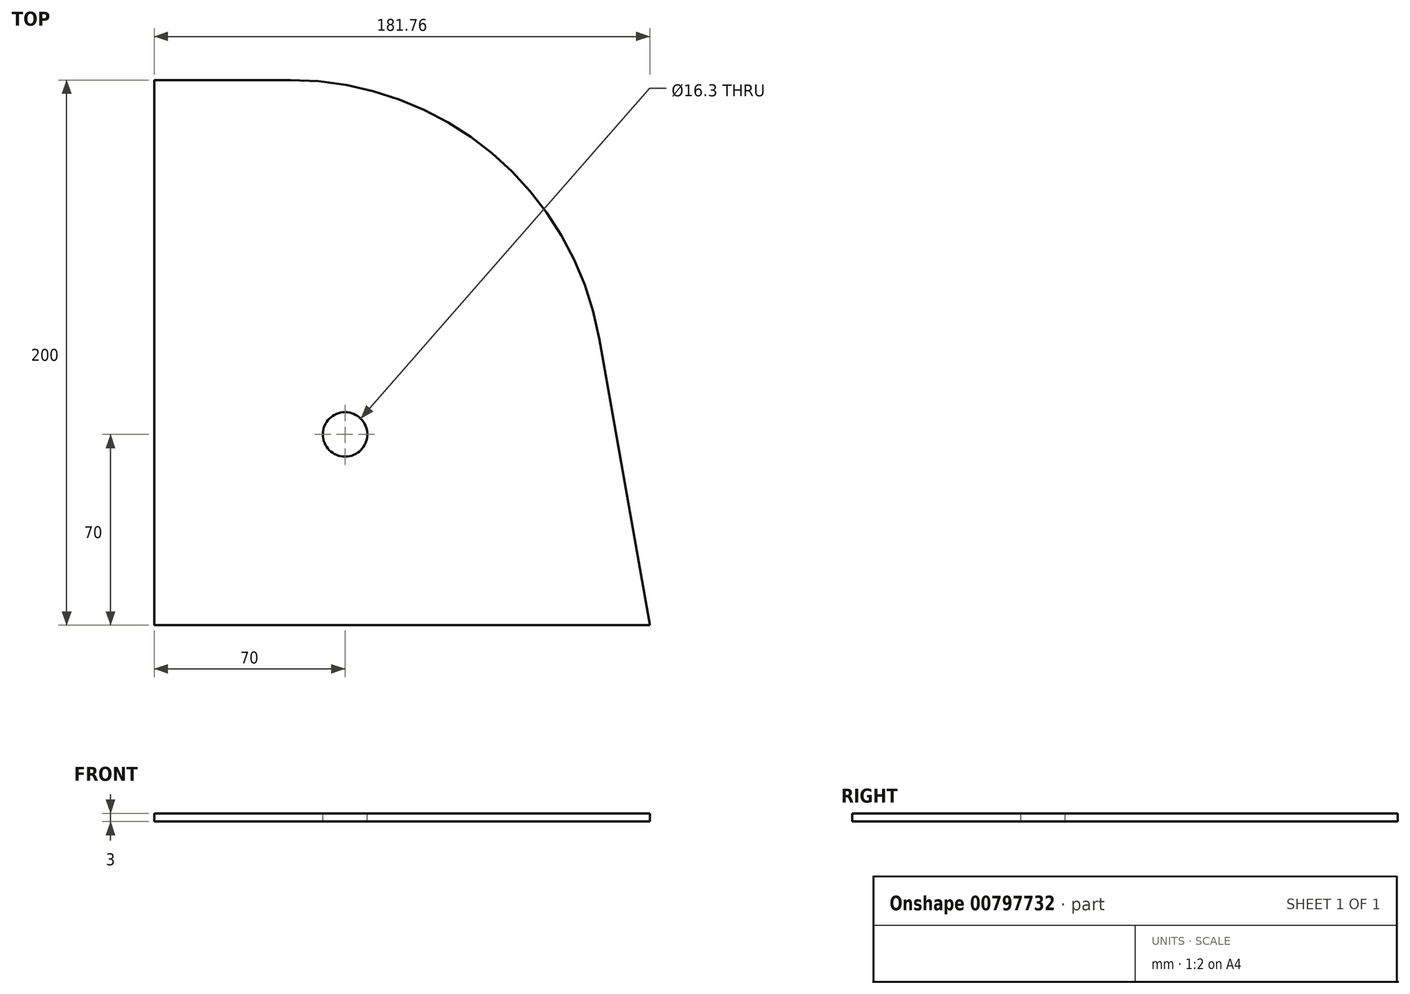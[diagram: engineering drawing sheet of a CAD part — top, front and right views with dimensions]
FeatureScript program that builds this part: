
annotation { "Feature Type Name" : "Feature", "Feature Type Description" : "" }
export const myFeature = defineFeature(function(context is Context, id is Id, definition is map)
    precondition{}
    {
        {
            var Q0;
            Q0=qCreatedBy(makeId("Top.planeOp"),FACE);
            var sketch = newSketch(context, id + "F0", { "sketchPlane" : qUnion([Q0])});
            skLineSegment(sketch, "E0", {"start": v(0, 0) * mm, "end": v(0, 200) * mm});
            skLineSegment(sketch, "E1", {"start": v(0, 0) * mm, "end": v(181.76, 0) * mm});
            skLineSegment(sketch, "E2", {"start": v(181.76, 0) * mm, "end": v(163.25, 104.97) * mm});
            skLineSegment(sketch, "E3", {"start": v(0, 200) * mm, "end": v(50, 200) * mm});
            skArc(sketch, "E4", {"start": v(163.25, 104.97) * mm, "mid": v(123.92, 173.1) * mm, "end": v(50, 200) * mm});
            skSolve(sketch);
        }
        {
            var Q0;
            Q0 = qSketchRegion(id + "F0", true);
            extrude(context, id + "F1", {"entities" : qUnion([Q0]), "depth" : 3 * mm, "offsetDistance" : 25 * mm});
        }
        {
            var Q0;
            Q0=makeQuery(id+"F1.opExtrude","CAP_FACE",FACE,{"disambiguationData":[OSD([sQuery(id+"F0.wireOp",EDGE,"E0"),sQuery(id+"F0.wireOp",EDGE,"E1"),sQuery(id+"F0.wireOp",EDGE,"E2"),sQuery(id+"F0.wireOp",EDGE,"E3"),sQuery(id+"F0.wireOp",EDGE,"E4")])],"isStart":false});
            var sketch = newSketch(context, id + "F2", { "sketchPlane" : qUnion([Q0])});
            skCircle(sketch, "E5", {"center": v(70, 70) * mm, "radius": 8.15 * mm});
            skSolve(sketch);
        }
        {
            var Q0;
            Q0 = qSketchRegion(id + "F2", true);
            extrude(context, id + "F3", {"entities" : qUnion([Q0]), "operationType" : NewBodyOperationType.REMOVE, "oppositeDirection" : true, "depth" : 25 * mm, "offsetDistance" : 25 * mm});
        }
    });
